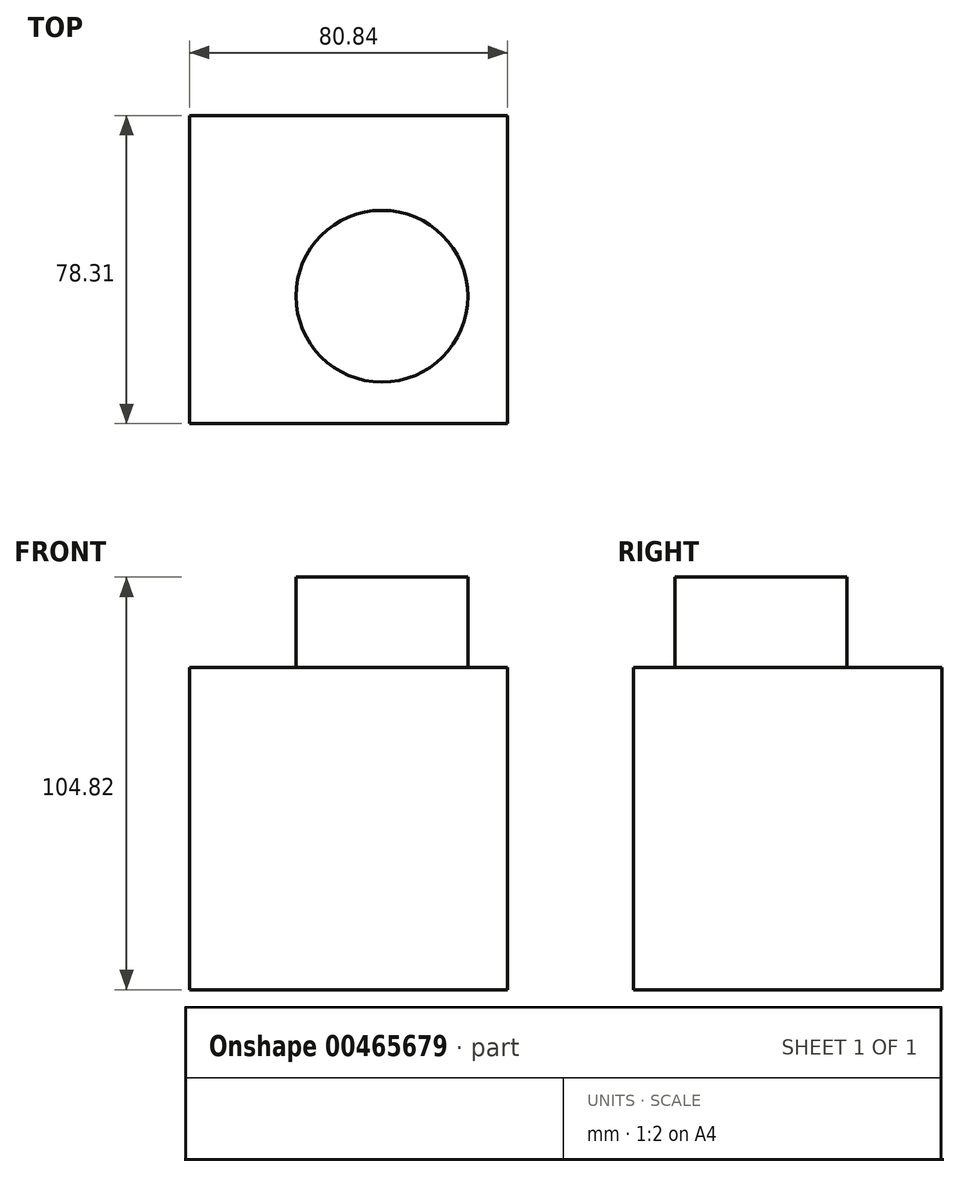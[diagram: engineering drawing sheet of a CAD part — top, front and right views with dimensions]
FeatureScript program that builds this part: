
annotation { "Feature Type Name" : "Feature", "Feature Type Description" : "" }
export const myFeature = defineFeature(function(context is Context, id is Id, definition is map)
    precondition{}
    {
        {
            var Q0;
            Q0=qCreatedBy(makeId("Right.planeOp"),FACE);
            var sketch = newSketch(context, id + "F0", { "sketchPlane" : qUnion([Q0])});
            skLineSegment(sketch, "E0.bottom", {"start": v(45.95, -55.14) * mm, "end": v(-32.36, -55.14) * mm});
            skLineSegment(sketch, "E0.top", {"start": v(45.95, 26.72) * mm, "end": v(-32.36, 26.72) * mm});
            skLineSegment(sketch, "E0.left", {"start": v(45.95, -55.14) * mm, "end": v(45.95, 26.72) * mm});
            skLineSegment(sketch, "E0.right", {"start": v(-32.36, -55.14) * mm, "end": v(-32.36, 26.72) * mm});
            skSolve(sketch);
        }
        {
            var Q0;
            Q0 = qSketchRegion(id + "F0", true);
            extrude(context, id + "F1", {"entities" : qUnion([Q0]), "depth" : 80.84 * mm});
        }
        {
            var Q0;
            Q0=makeQuery(id+"F1.opExtrude","SWEPT_FACE",FACE,{"disambiguationData":[OSD([sQuery(id+"F0.wireOp",EDGE,"E0.top")])]});
            var sketch = newSketch(context, id + "F2", { "sketchPlane" : qUnion([Q0])});
            skCircle(sketch, "E1", {"center": v(48.86, 0) * mm, "radius": 21.82 * mm});
            skSolve(sketch);
        }
        {
            var Q0;
            Q0=makeQuery(id+"F2.imprint","IMPRINT",FACE,{"disambiguationData":[TD([[makeQuery(id+"F2.imprint","IMPRINT",EDGE,{"derivedFrom":sQuery(id+"F2.wireOp",EDGE,"E1")}),1.0]])]});
            extrude(context, id + "F3", {"entities" : qUnion([Q0]), "operationType" : NewBodyOperationType.ADD, "depth" : 22.96 * mm});
        }
    });
